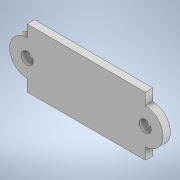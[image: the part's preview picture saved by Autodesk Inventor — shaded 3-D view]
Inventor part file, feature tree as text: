
AUTODESK INVENTOR PART (.ipt)
format: ipt  version: 2020 (Build 240168000, 168)  size: 113,152 bytes
history: native  units: in
note: dims shown in document units (in); Inventor stores cm internally (conversion verified against a paired STEP export)
features: extrude x2, sketch x2
ambient origin geometry x8: Origin, YZ Plane, XZ Plane, XY Plane, X Axis, Y Axis, Z Axis, Center Point
bodies: Solid1 (feature_tree)
feature tree (4):
  extrude  "Extrusion1"  Depth=1.0in
  extrude  "Extrusion2"  Depth=0.125in TaperAngle=0.0deg
  sketch  "Sketch1"  dims[d0=2.0in d1=1.0in]
  sketch  "Sketch2"  dims[d2=0.6in d3=0.125in d4=0.0in d5=0.203in d6=0.0in d7=0.0in]
